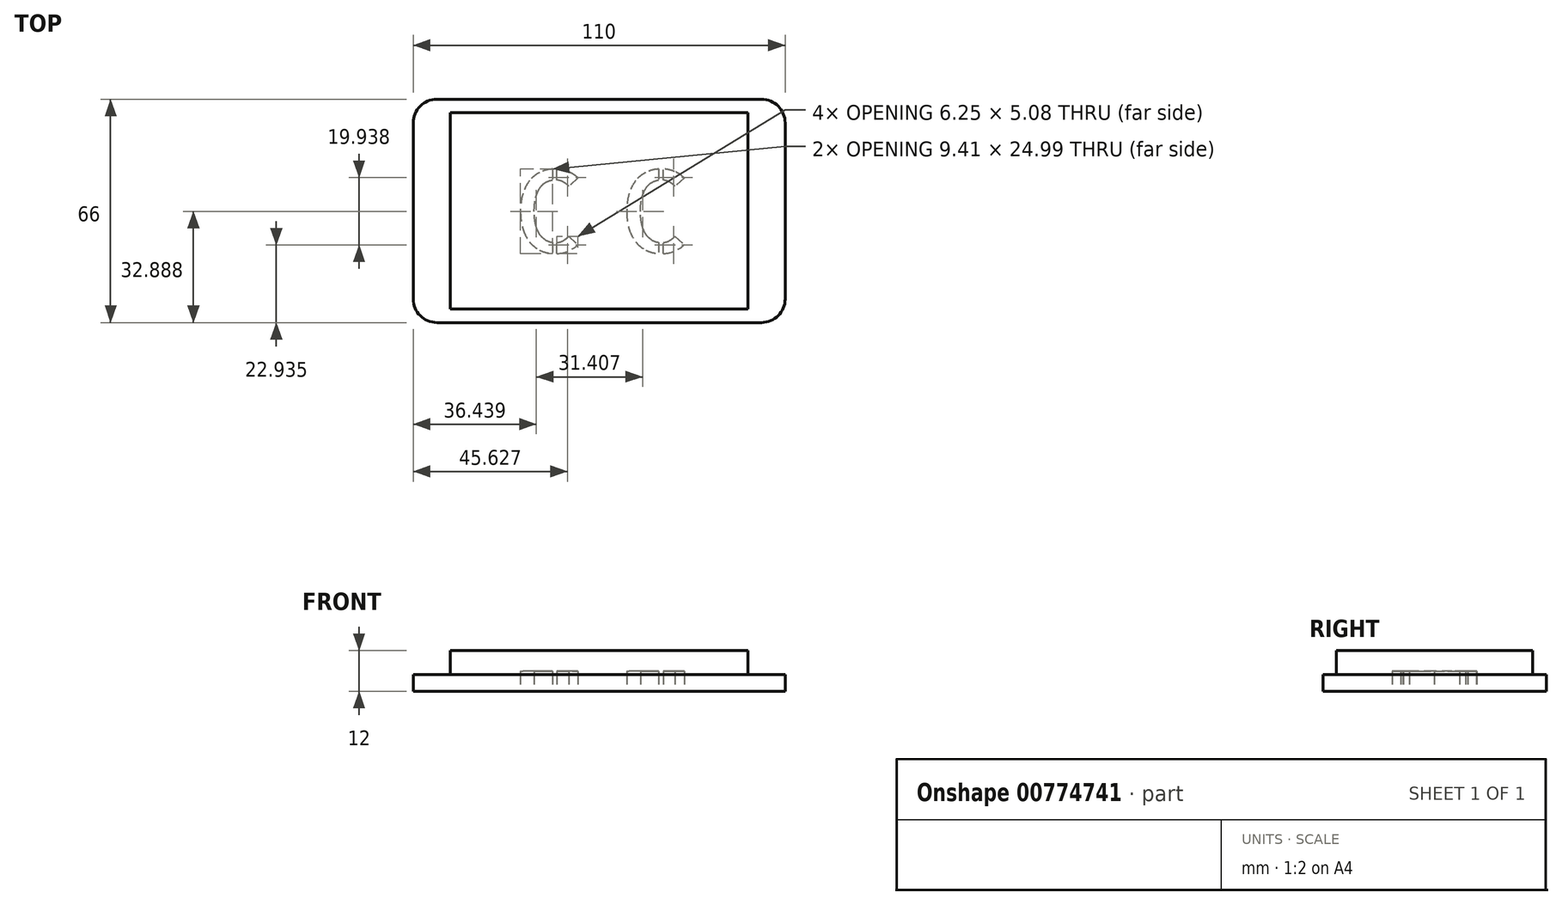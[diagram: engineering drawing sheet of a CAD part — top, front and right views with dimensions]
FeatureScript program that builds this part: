
annotation { "Feature Type Name" : "Feature", "Feature Type Description" : "" }
export const myFeature = defineFeature(function(context is Context, id is Id, definition is map)
    precondition{}
    {
        {
            var Q0;
            Q0=qCreatedBy(makeId("Top.planeOp"),FACE);
            var sketch = newSketch(context, id + "F0", { "sketchPlane" : qUnion([Q0])});
            skLineSegment(sketch, "E0.bottom", {"start": v(55, -33) * mm, "end": v(-55, -33) * mm});
            skLineSegment(sketch, "E0.top", {"start": v(55, 33) * mm, "end": v(-55, 33) * mm});
            skLineSegment(sketch, "E0.left", {"start": v(55, -33) * mm, "end": v(55, 33) * mm});
            skLineSegment(sketch, "E0.right", {"start": v(-55, -33) * mm, "end": v(-55, 33) * mm});
            skPoint(sketch, "E0.middle", {"position": v(0, 0) * mm});
            skSolve(sketch);
        }
        {
            var Q0;
            Q0=makeQuery(id+"F0.imprint","IMPRINT",FACE,{"disambiguationData":[TD([[makeQuery(id+"F0.imprint","IMPRINT",EDGE,{"derivedFrom":sQuery(id+"F0.wireOp",EDGE,"E0.bottom")}),-1.0]])]});
            extrude(context, id + "F1", {"entities" : qUnion([Q0]), "depth" : 5 * mm, "offsetDistance" : 25 * mm});
        }
        {
            var Q0;
            Q0=makeQuery(id+"F1.opExtrude","CAP_FACE",FACE,{"disambiguationData":[OSD([sQuery(id+"F0.wireOp",EDGE,"E0.bottom"),sQuery(id+"F0.wireOp",EDGE,"E0.top"),sQuery(id+"F0.wireOp",EDGE,"E0.left"),sQuery(id+"F0.wireOp",EDGE,"E0.right")])],"isStart":false});
            var sketch = newSketch(context, id + "F2", { "sketchPlane" : qUnion([Q0])});
            skLineSegment(sketch, "E1.bottom", {"start": v(44, -29) * mm, "end": v(-44, -29) * mm});
            skLineSegment(sketch, "E1.top", {"start": v(44, 29) * mm, "end": v(-44, 29) * mm});
            skLineSegment(sketch, "E1.left", {"start": v(44, -29) * mm, "end": v(44, 29) * mm});
            skLineSegment(sketch, "E1.right", {"start": v(-44, -29) * mm, "end": v(-44, 29) * mm});
            skPoint(sketch, "E1.middle", {"position": v(0, 0) * mm});
            skSolve(sketch);
        }
        {
            var Q0;
            Q0=makeQuery(id+"F2.imprint","IMPRINT",FACE,{"disambiguationData":[TD([[makeQuery(id+"F2.imprint","IMPRINT",EDGE,{"derivedFrom":sQuery(id+"F2.wireOp",EDGE,"E1.bottom")}),-1.0]])]});
            extrude(context, id + "F3", {"entities" : qUnion([Q0]), "depth" : 7 * mm, "offsetDistance" : 25 * mm});
        }
        {
            var Q0;
            Q0=makeQuery(id+"F1.opExtrude","CAP_FACE",FACE,{"disambiguationData":[OSD([sQuery(id+"F0.wireOp",EDGE,"E0.bottom"),sQuery(id+"F0.wireOp",EDGE,"E0.top"),sQuery(id+"F0.wireOp",EDGE,"E0.left"),sQuery(id+"F0.wireOp",EDGE,"E0.right")])],"isStart":true});
            var sketch = newSketch(context, id + "F4", { "sketchPlane" : qUnion([Q0])});
            skText(sketch, "E2", { "text": "C C", "fontName": "AllertaStencil-Regular.ttf"});
            const initialGuessF4  = {"E2": [-0.02589, -0.01225, 1, 0, 0.0245]};
            skSetInitialGuess(sketch, initialGuessF4);
            skSolve(sketch);
        }
        {
            var Q0;
            Q0 = qSketchRegion(id + "F4", true);
            extrude(context, id + "F5", {"entities" : qUnion([Q0]), "operationType" : NewBodyOperationType.REMOVE, "oppositeDirection" : true, "depth" : 6 * mm, "offsetDistance" : 25 * mm});
        }
        {
            var Q0;
            Q0 = qSketchRegion(id + "F4", true);
            extrude(context, id + "F6", {"entities" : qUnion([Q0]), "operationType" : NewBodyOperationType.REMOVE, "oppositeDirection" : true, "depth" : 6 * mm, "offsetDistance" : 25 * mm});
        }
        {
            var Q0;
            Q0=makeQuery(id+"F1.opExtrude","SWEPT_EDGE",EDGE,{"disambiguationData":[OSD([sQuery(id+"F0.wireOp",EDGE,"E0.bottom"),sQuery(id+"F0.wireOp",EDGE,"E0.left")])]});
            fillet(context, id + "F7", {"entities" : qUnion([Q0]), "radius" : 7 * mm, "tangentPropagation" : true, "allowEdgeOverflow" : false});
        }
        {
            var Q0;
            Q0=makeQuery(id+"F1.opExtrude","SWEPT_EDGE",EDGE,{"disambiguationData":[OSD([sQuery(id+"F0.wireOp",EDGE,"E0.top"),sQuery(id+"F0.wireOp",EDGE,"E0.left")])]});
            fillet(context, id + "F8", {"entities" : qUnion([Q0]), "radius" : 7 * mm, "tangentPropagation" : true, "allowEdgeOverflow" : false});
        }
        {
            var Q0;
            Q0=makeQuery(id+"F1.opExtrude","SWEPT_EDGE",EDGE,{"disambiguationData":[OSD([sQuery(id+"F0.wireOp",EDGE,"E0.top"),sQuery(id+"F0.wireOp",EDGE,"E0.right")])]});
            fillet(context, id + "F9", {"entities" : qUnion([Q0]), "radius" : 7 * mm, "tangentPropagation" : true, "allowEdgeOverflow" : false});
        }
        {
            var Q0;
            Q0=makeQuery(id+"F1.opExtrude","SWEPT_EDGE",EDGE,{"disambiguationData":[OSD([sQuery(id+"F0.wireOp",EDGE,"E0.bottom"),sQuery(id+"F0.wireOp",EDGE,"E0.right")])]});
            fillet(context, id + "F10", {"entities" : qUnion([Q0]), "radius" : 7 * mm, "tangentPropagation" : true, "allowEdgeOverflow" : false});
        }
    });
